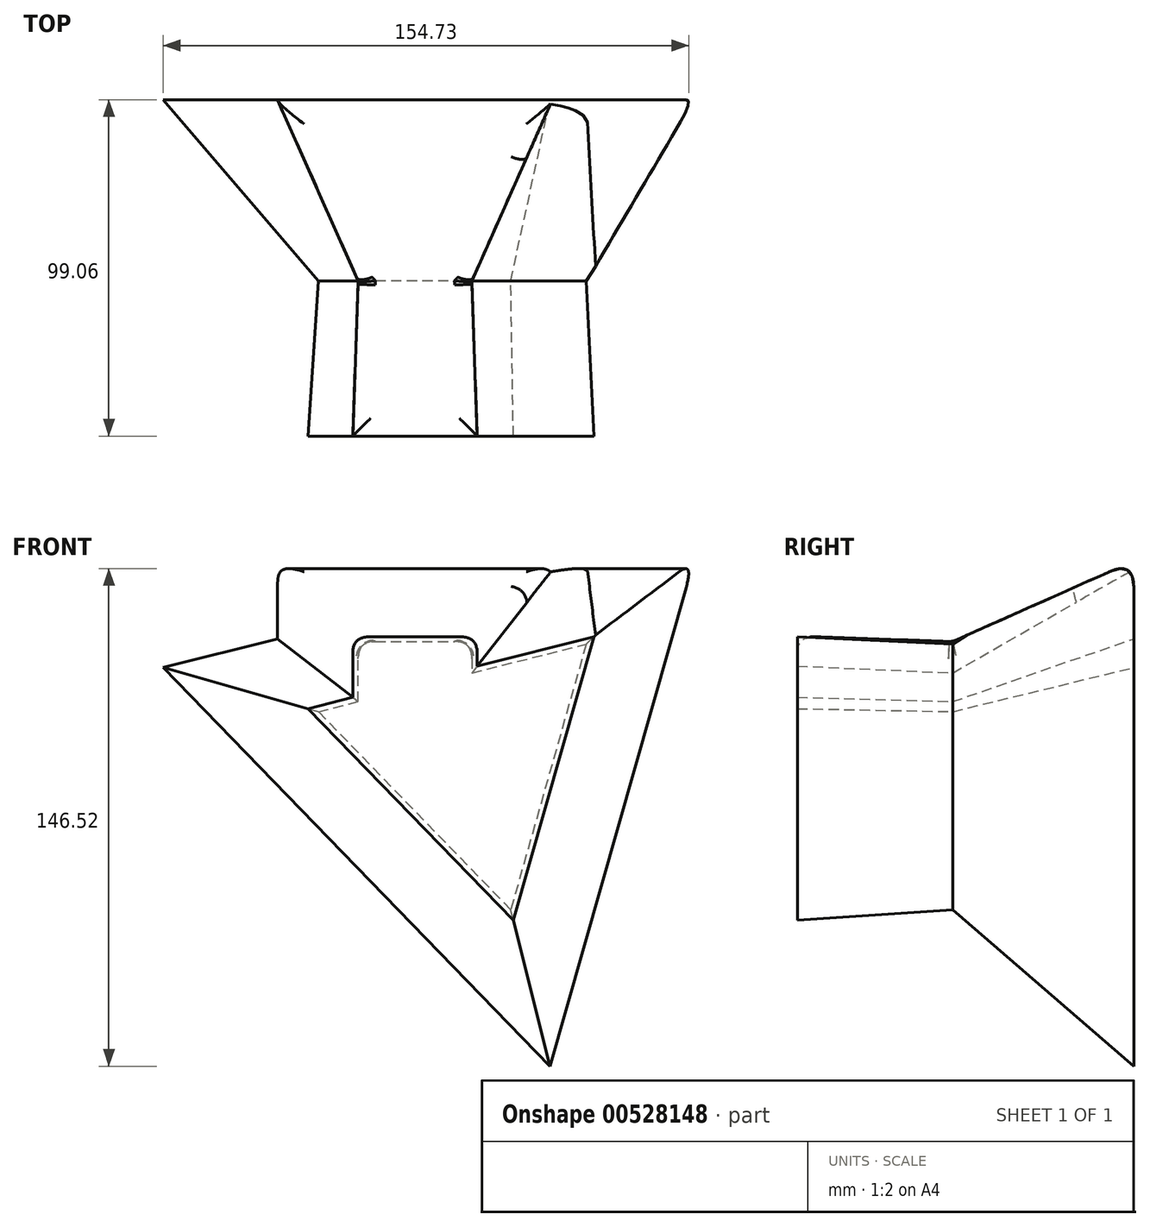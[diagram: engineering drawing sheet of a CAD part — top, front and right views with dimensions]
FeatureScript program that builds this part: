
annotation { "Feature Type Name" : "Feature", "Feature Type Description" : "" }
export const myFeature = defineFeature(function(context is Context, id is Id, definition is map)
    precondition{}
    {
        {
            var Q0;
            Q0=qCreatedBy(makeId("Front.planeOp"),FACE);
            var sketch = newSketch(context, id + "F0", { "sketchPlane" : qUnion([Q0])});
            skCircle(sketch, "E0.cCircle", {"center": v(-39.3, 23.14) * mm, "radius": 16.73 * mm, "construction": true});
            skLineSegment(sketch, "E0.0", {"start": v(-22.58, 39.87) * mm, "end": v(-22.58, 6.41) * mm});
            skLineSegment(sketch, "E0.1", {"start": v(-22.58, 6.41) * mm, "end": v(-56.03, 6.41) * mm});
            skLineSegment(sketch, "E0.2", {"start": v(-56.03, 6.41) * mm, "end": v(-56.03, 39.87) * mm});
            skLineSegment(sketch, "E0.3", {"start": v(-56.03, 39.87) * mm, "end": v(-22.58, 39.87) * mm});
            skPoint(sketch, "E0.0.midPoint", {"position": v(-22.58, 23.14) * mm});
            skCircle(sketch, "E1.cCircle", {"center": v(-22.58, 6.41) * mm, "radius": 23.47 * mm, "construction": true});
            skLineSegment(sketch, "E1.0", {"start": v(11.1, 39.11) * mm, "end": v(-11.1, -39.11) * mm});
            skLineSegment(sketch, "E1.1", {"start": v(-11.1, -39.11) * mm, "end": v(-67.74, 19.24) * mm});
            skLineSegment(sketch, "E1.2", {"start": v(-67.74, 19.24) * mm, "end": v(11.1, 39.11) * mm});
            skPoint(sketch, "E1.0.midPoint", {"position": v(0, 0) * mm});
            skSolve(sketch);
        }
        {
            var Q0;
            {var subQ1=sQuery(id+"F0.wireOp",EDGE,"E0.1");var subQ7=sQuery(id+"F0.wireOp",EDGE,"E0.0");var subQ8=makeQuery(id+"F0.imprint","INTERSECT",VERTEX,{"derivedFrom":[subQ7,subQ1]});Q0=makeQuery(id+"F0.imprint","IMPRINT",FACE,{"disambiguationData":[TD([[makeQuery(id+"F0.imprint","IMPRINT",EDGE,{"disambiguationData":[TD([[subQ8,1.0]])],"derivedFrom":subQ7}),-1.0]])]});}
            var Q1;
            {var subQ0=sQuery(id+"F0.wireOp",EDGE,"E0.3");Q1=makeQuery(id+"F0.imprint","IMPRINT",FACE,{"disambiguationData":[TD([[makeQuery(id+"F0.imprint","IMPRINT",EDGE,{"derivedFrom":subQ0}),-1.0]])]});}
            var Q2;
            {var subQ1=sQuery(id+"F0.wireOp",EDGE,"E1.0");Q2=makeQuery(id+"F0.imprint","IMPRINT",FACE,{"disambiguationData":[TD([[makeQuery(id+"F0.imprint","IMPRINT",EDGE,{"derivedFrom":subQ1}),-1.0]])]});}
            var Q3;
            {var subQ0=sQuery(id+"F0.wireOp",EDGE,"E1.1");var subQ1=sQuery(id+"F0.wireOp",EDGE,"E0.2");var subQ2=makeQuery(id+"F0.imprint","INTERSECT",VERTEX,{"derivedFrom":[subQ1,subQ0]});Q3=makeQuery(id+"F0.imprint","IMPRINT",FACE,{"disambiguationData":[TD([[makeQuery(id+"F0.imprint","IMPRINT",EDGE,{"disambiguationData":[TD([[subQ2,-1.0]])],"derivedFrom":subQ1}),1.0]])]});}
            extrude(context, id + "F1", {"entities" : qUnion([Q0, Q1, Q2, Q3]), "depth" : 45.72 * mm, "offsetDistance" : 25.4 * mm, "hasDraft" : true, "draftAngle" : 2 * degree, "hasSecondDirection" : true, "secondDirectionOppositeDirection" : true, "secondDirectionDepth" : 53.34 * mm, "hasSecondDirectionDraft" : true, "secondDirectionDraftAngle" : 24 * degree});
        }
        {
            var Q0;
            Q0=makeQuery(id+"F1.opExtrude","CAP_EDGE",EDGE,{"disambiguationData":[OSD([sQuery(id+"F0.wireOp",EDGE,"E0.3")])],"isStart":false});
            var Q1;
            Q1=makeQuery(id+"F1.*.split.splitOp","SPLIT",EDGE,{"derivedFrom":makeQuery(id+"F1.opExtrude","SWEPT_EDGE",EDGE,{"disambiguationData":[OSD([sQuery(id+"F0.wireOp",EDGE,"E0.2"),sQuery(id+"F0.wireOp",EDGE,"E0.3")])]}),"isFromBackBody":true});
            var Q2;
            Q2=makeQuery(id+"F1.opExtrude","CAP_EDGE",EDGE,{"disambiguationData":[OSD([sQuery(id+"F0.wireOp",EDGE,"E0.3")])],"isStart":true});
            var Q3;
            Q3=makeQuery(id+"F1.*.split.splitOp","SPLIT",EDGE,{"derivedFrom":makeQuery(id+"F1.opExtrude","SWEPT_EDGE",EDGE,{"disambiguationData":[OSD([sQuery(id+"F0.wireOp",EDGE,"E0.0"),sQuery(id+"F0.wireOp",EDGE,"E0.3")])]}),"isFromBackBody":true});
            var Q4;
            {var subQ0=makeQuery(id+"F1.opExtrude","SWEPT_FACE",FACE,{"disambiguationData":[OSD([sQuery(id+"F0.wireOp",EDGE,"E0.3")])]});Q4=makeQuery(id+"F1.*.booleanUnion.opBoolean","MERGE",EDGE,{"derivedFrom":[makeQuery(id+"F1.*.split.splitOp","SPLIT_SURFACE_INTERSECT",EDGE,{"derivedFrom":[subQ0]}),makeQuery(id+"F1.*.split.splitOp","SPLIT_SURFACE_INTERSECT",EDGE,{"derivedFrom":[subQ0],"isFromBackBody":true})]});}
            var Q5;
            Q5=makeQuery(id+"F1.*.split.splitOp","SPLIT",EDGE,{"derivedFrom":makeQuery(id+"F1.opExtrude","SWEPT_EDGE",EDGE,{"disambiguationData":[OSD([sQuery(id+"F0.wireOp",EDGE,"E0.2"),sQuery(id+"F0.wireOp",EDGE,"E0.3")])]})});
            var Q6;
            Q6=makeQuery(id+"F1.*.split.splitOp","SPLIT",EDGE,{"derivedFrom":makeQuery(id+"F1.opExtrude","SWEPT_EDGE",EDGE,{"disambiguationData":[OSD([sQuery(id+"F0.wireOp",EDGE,"E0.0"),sQuery(id+"F0.wireOp",EDGE,"E0.3")])]})});
            fillet(context, id + "F2", {"entities" : qUnion([Q0, Q1, Q2, Q3, Q4, Q5, Q6]), "radius" : 5.08 * mm, "tangentPropagation" : true, "rho" : 0.5, "crossSection" : FilletCrossSection.CONIC, "allowEdgeOverflow" : false});
        }
    });
